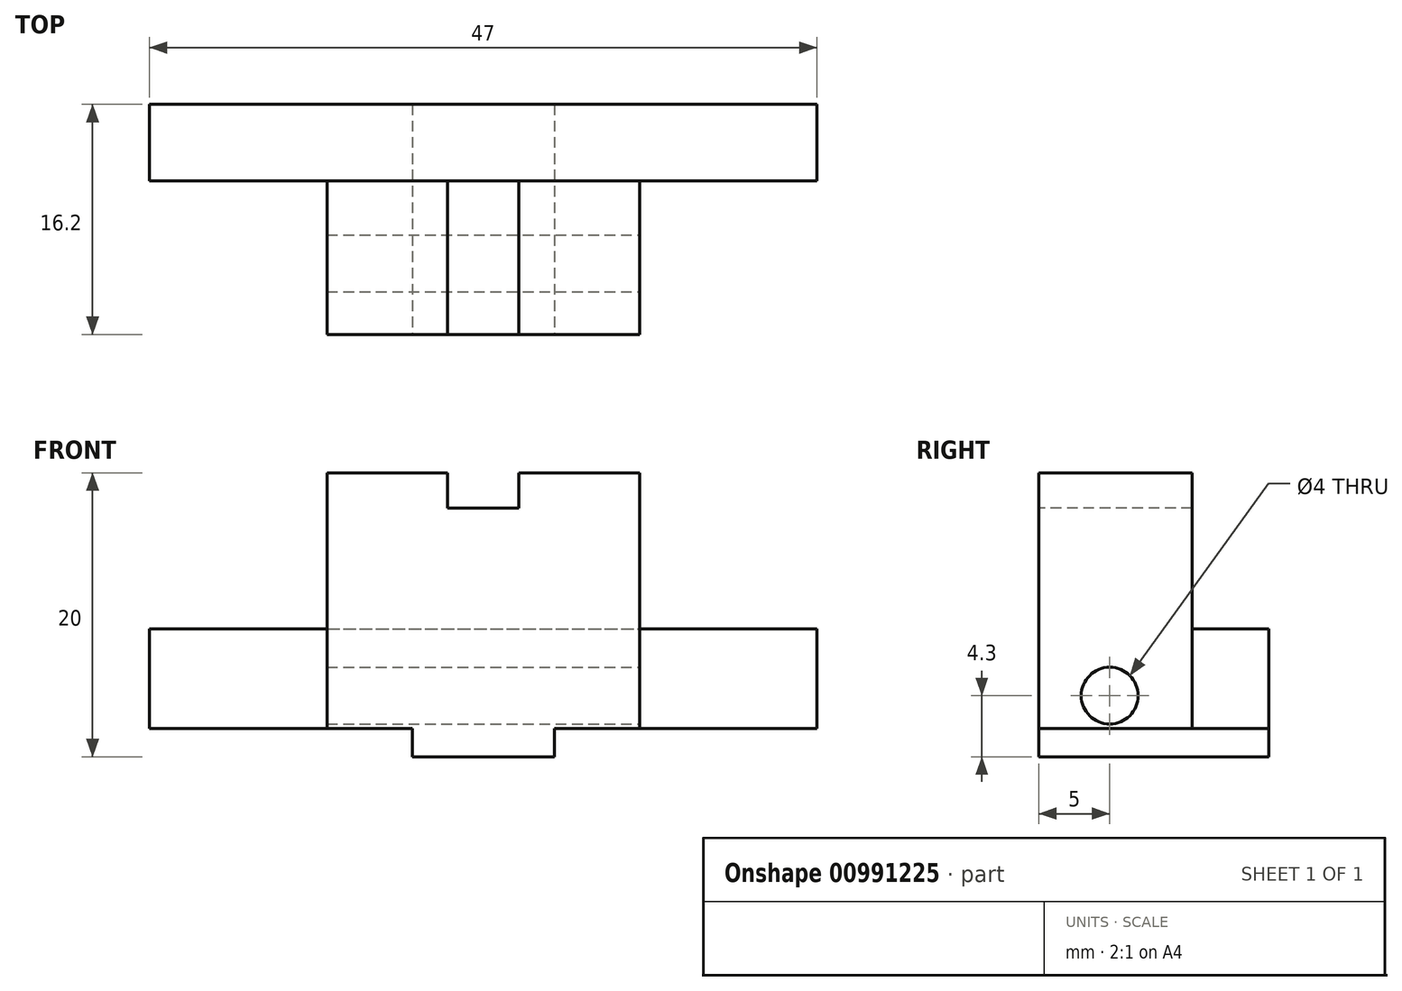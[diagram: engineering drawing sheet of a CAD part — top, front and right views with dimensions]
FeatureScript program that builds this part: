
annotation { "Feature Type Name" : "Feature", "Feature Type Description" : "" }
export const myFeature = defineFeature(function(context is Context, id is Id, definition is map)
    precondition{}
    {
        {
            var Q0;
            Q0=qCreatedBy(makeId("Top.planeOp"),FACE);
            var sketch = newSketch(context, id + "F0", { "sketchPlane" : qUnion([Q0])});
            skLineSegment(sketch, "E0", {"start": v(0, 0) * mm, "end": v(23.5, 0) * mm});
            skLineSegment(sketch, "E1", {"start": v(23.5, 0) * mm, "end": v(23.5, -5.4) * mm});
            skLineSegment(sketch, "E2", {"start": v(23.5, -5.4) * mm, "end": v(11, -5.4) * mm});
            skLineSegment(sketch, "E3", {"start": v(11, -5.4) * mm, "end": v(11, -16.2) * mm});
            skLineSegment(sketch, "E4", {"start": v(11, -16.2) * mm, "end": v(0, -16.2) * mm});
            skLineSegment(sketch, "E5.MirrorCS", {"start": v(-11, -16.2) * mm, "end": v(0, -16.2) * mm});
            skLineSegment(sketch, "E6.MirrorCS", {"start": v(-11, -5.4) * mm, "end": v(-11, -16.2) * mm});
            skLineSegment(sketch, "E7.MirrorCS", {"start": v(-23.5, -5.4) * mm, "end": v(-11, -5.4) * mm});
            skLineSegment(sketch, "E8.MirrorCS", {"start": v(0, 0) * mm, "end": v(-23.5, 0) * mm});
            skLineSegment(sketch, "E9.MirrorCS", {"start": v(-23.5, 0) * mm, "end": v(-23.5, -5.4) * mm});
            skLineSegment(sketch, "E10", {"start": v(-11, -5.4) * mm, "end": v(-11, 0) * mm});
            skLineSegment(sketch, "E11", {"start": v(11, -5.4) * mm, "end": v(11, 0) * mm});
            skPoint(sketch, "E11.endSnap0", {"position": v(11.75, 0) * mm});
            skSolve(sketch);
        }
        {
            var Q0;
            Q0 = qSketchRegion(id + "F0", true);
            extrude(context, id + "F1", {"entities" : qUnion([Q0]), "depth" : 18 * mm, "offsetDistance" : 25 * mm});
        }
        {
            var Q0;
            Q0=makeQuery(id+"F1.opExtrude","SWEPT_FACE",FACE,{"disambiguationData":[OSD([sQuery(id+"F0.wireOp",EDGE,"E3")])]});
            var sketch = newSketch(context, id + "F2", { "sketchPlane" : qUnion([Q0])});
            skLineSegment(sketch, "E12", {"start": v(-16.2, 0) * mm, "end": v(-11.2, 0) * mm, "construction": true});
            skLineSegment(sketch, "E13", {"start": v(-11.2, 0) * mm, "end": v(-11.2, 2.3) * mm, "construction": true});
            skCircle(sketch, "E14", {"center": v(-11.2, 2.3) * mm, "radius": 2 * mm});
            skSolve(sketch);
        }
        {
            var Q0;
            Q0=makeQuery(id+"F2.imprint","IMPRINT",FACE,{"disambiguationData":[TD([[makeQuery(id+"F2.imprint","IMPRINT",EDGE,{"derivedFrom":sQuery(id+"F2.wireOp",EDGE,"E14")}),1.0]])]});
            extrude(context, id + "F3", {"entities" : qUnion([Q0]), "operationType" : NewBodyOperationType.REMOVE, "endBound" : BoundingType.THROUGH_ALL, "oppositeDirection" : true, "depth" : 25 * mm, "offsetDistance" : 25 * mm});
        }
        {
            var Q0;
            Q0=makeQuery(id+"F1.opExtrude","CAP_FACE",FACE,{"disambiguationData":[OSD([sQuery(id+"F0.wireOp",EDGE,"E0"),sQuery(id+"F0.wireOp",EDGE,"E1"),sQuery(id+"F0.wireOp",EDGE,"E2"),sQuery(id+"F0.wireOp",EDGE,"E3"),sQuery(id+"F0.wireOp",EDGE,"E4"),sQuery(id+"F0.wireOp",EDGE,"E5.MirrorCS"),sQuery(id+"F0.wireOp",EDGE,"E6.MirrorCS"),sQuery(id+"F0.wireOp",EDGE,"E7.MirrorCS"),sQuery(id+"F0.wireOp",EDGE,"E8.MirrorCS"),sQuery(id+"F0.wireOp",EDGE,"E9.MirrorCS")])],"isStart":true});
            var sketch = newSketch(context, id + "F4", { "sketchPlane" : qUnion([Q0])});
            skLineSegment(sketch, "E15", {"start": v(11, 5.4) * mm, "end": v(11, 0) * mm});
            skLineSegment(sketch, "E16", {"start": v(11, 0) * mm, "end": v(23.5, 0) * mm});
            skLineSegment(sketch, "E17", {"start": v(23.5, 0) * mm, "end": v(23.5, 5.4) * mm});
            skLineSegment(sketch, "E18", {"start": v(23.5, 5.4) * mm, "end": v(11, 5.4) * mm});
            skLineSegment(sketch, "E19", {"start": v(0, 0) * mm, "end": v(0, 16.2) * mm, "construction": true});
            skLineSegment(sketch, "E20.MirrorCS", {"start": v(-23.5, 0) * mm, "end": v(-23.5, 5.4) * mm});
            skLineSegment(sketch, "E21.MirrorCS", {"start": v(-11, 0) * mm, "end": v(-23.5, 0) * mm});
            skLineSegment(sketch, "E22.MirrorCS", {"start": v(-23.5, 5.4) * mm, "end": v(-11, 5.4) * mm});
            skLineSegment(sketch, "E23.MirrorCS", {"start": v(-11, 5.4) * mm, "end": v(-11, 0) * mm});
            skLineSegment(sketch, "E24.bottom", {"start": v(0, 0) * mm, "end": v(5, 0) * mm});
            skLineSegment(sketch, "E24.top", {"start": v(0, 16.2) * mm, "end": v(5, 16.2) * mm});
            skLineSegment(sketch, "E24.left", {"start": v(0, 0) * mm, "end": v(0, 16.2) * mm});
            skLineSegment(sketch, "E24.right", {"start": v(5, 0) * mm, "end": v(5, 16.2) * mm});
            skLineSegment(sketch, "E25.MirrorCS", {"start": v(0, 16.2) * mm, "end": v(-5, 16.2) * mm});
            skLineSegment(sketch, "E26.MirrorCS", {"start": v(0, 0) * mm, "end": v(-5, 0) * mm});
            skLineSegment(sketch, "E27.MirrorCS", {"start": v(-5, 0) * mm, "end": v(-5, 16.2) * mm});
            skSolve(sketch);
        }
        {
            var Q0;
            Q0=makeQuery(id+"F4.imprint","IMPRINT",FACE,{"disambiguationData":[TD([[makeQuery(id+"F4.imprint","IMPRINT",EDGE,{"derivedFrom":sQuery(id+"F4.wireOp",EDGE,"E24.bottom")}),1.0]])]});
            var Q1;
            Q1=makeQuery(id+"F4.imprint","IMPRINT",FACE,{"disambiguationData":[TD([[makeQuery(id+"F4.imprint","IMPRINT",EDGE,{"derivedFrom":sQuery(id+"F4.wireOp",EDGE,"E24.left")}),1.0]])]});
            extrude(context, id + "F5", {"entities" : qUnion([Q0, Q1]), "operationType" : NewBodyOperationType.ADD, "depth" : 2 * mm, "offsetDistance" : 25 * mm});
        }
        {
            var Q0;
            Q0=makeQuery(id+"F1.opExtrude","SWEPT_FACE",FACE,{"disambiguationData":[OSD([sQuery(id+"F0.wireOp",EDGE,"E1")])]});
            var sketch = newSketch(context, id + "F6", { "sketchPlane" : qUnion([Q0])});
            skLineSegment(sketch, "E28", {"start": v(0, 0) * mm, "end": v(0, 7) * mm});
            skLineSegment(sketch, "E29", {"start": v(0, 7) * mm, "end": v(-5.4, 7) * mm});
            skLineSegment(sketch, "E30", {"start": v(-5.4, 7) * mm, "end": v(-5.4, 0) * mm});
            skLineSegment(sketch, "E31", {"start": v(-5.4, 0) * mm, "end": v(0, 0) * mm});
            skSolve(sketch);
        }
        {
            var Q0;
            {var subQ0=sQuery(id+"F6.wireOp",EDGE,"E29");Q0=makeQuery(id+"F6.imprint","IMPRINT",FACE,{"disambiguationData":[TD([[makeQuery(id+"F6.imprint","IMPRINT",EDGE,{"derivedFrom":subQ0}),-1.0]])]});}
            extrude(context, id + "F7", {"entities" : qUnion([Q0]), "operationType" : NewBodyOperationType.REMOVE, "endBound" : BoundingType.THROUGH_ALL, "oppositeDirection" : true, "depth" : 25 * mm, "offsetDistance" : 25 * mm});
        }
        {
            var Q0;
            Q0=makeQuery(id+"F5.boolean.opBoolean","MERGE",FACE,{"derivedFrom":[makeQuery(id+"F1.opExtrude","SWEPT_FACE",FACE,{"disambiguationData":[OSD([sQuery(id+"F0.wireOp",EDGE,"E4"),sQuery(id+"F0.wireOp",EDGE,"E5.MirrorCS")])]}),makeQuery(id+"F5.opExtrude","SWEPT_FACE",FACE,{"disambiguationData":[OSD([sQuery(id+"F4.wireOp",EDGE,"E24.top"),sQuery(id+"F4.wireOp",EDGE,"E25.MirrorCS")])]})]});
            var sketch = newSketch(context, id + "F8", { "sketchPlane" : qUnion([Q0])});
            skLineSegment(sketch, "E32", {"start": v(0, 18) * mm, "end": v(2.5, 18) * mm});
            skLineSegment(sketch, "E33", {"start": v(2.5, 18) * mm, "end": v(2.5, 15.5) * mm});
            skLineSegment(sketch, "E34", {"start": v(2.5, 15.5) * mm, "end": v(-2.5, 15.5) * mm});
            skLineSegment(sketch, "E35", {"start": v(-2.5, 15.5) * mm, "end": v(-2.5, 18) * mm});
            skLineSegment(sketch, "E36", {"start": v(-2.5, 18) * mm, "end": v(0, 18) * mm});
            skSolve(sketch);
        }
        {
            var Q0;
            Q0=makeQuery(id+"F8.imprint","IMPRINT",FACE,{"disambiguationData":[TD([[makeQuery(id+"F8.imprint","IMPRINT",EDGE,{"derivedFrom":sQuery(id+"F8.wireOp",EDGE,"E32")}),-1.0]])]});
            extrude(context, id + "F9", {"entities" : qUnion([Q0]), "operationType" : NewBodyOperationType.REMOVE, "endBound" : BoundingType.THROUGH_ALL, "oppositeDirection" : true, "depth" : 25 * mm, "offsetDistance" : 25 * mm});
        }
    });
